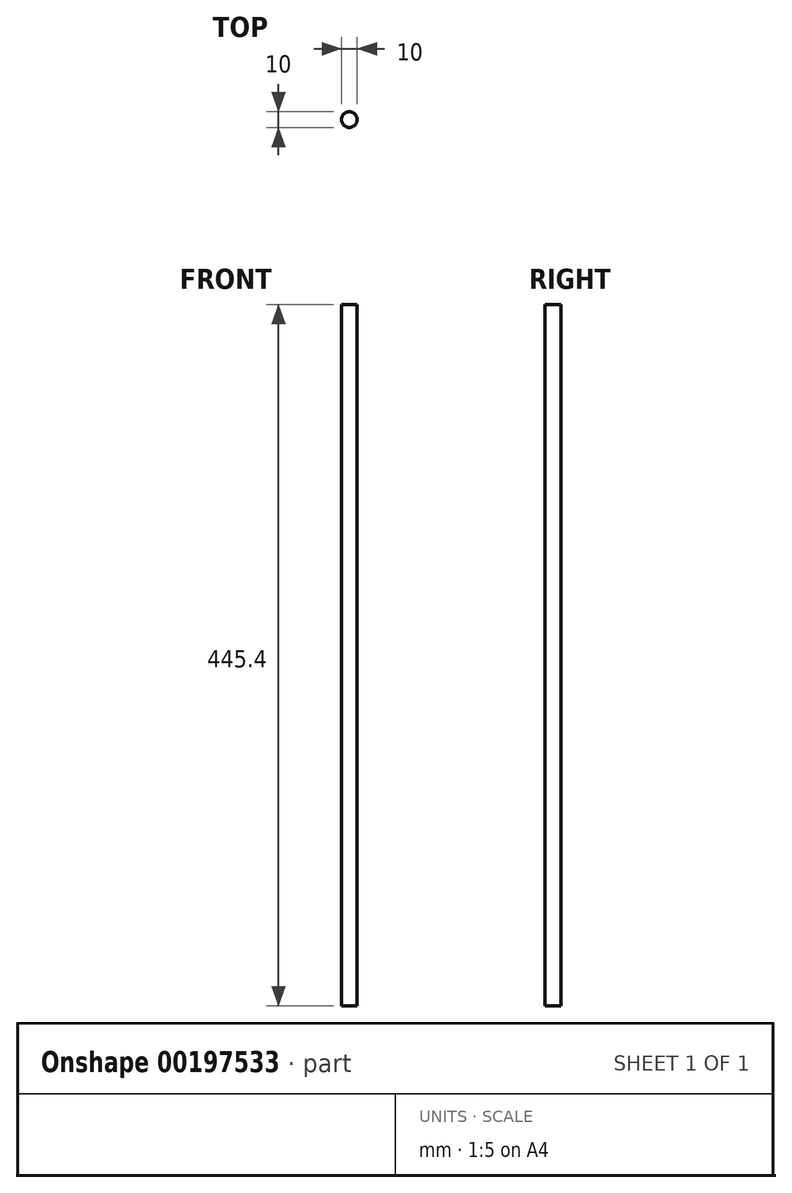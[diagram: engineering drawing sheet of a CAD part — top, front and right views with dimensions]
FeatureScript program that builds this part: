
annotation { "Feature Type Name" : "Feature", "Feature Type Description" : "" }
export const myFeature = defineFeature(function(context is Context, id is Id, definition is map)
    precondition{}
    {
        {
            var Q0;
            Q0=qCreatedBy(makeId("Top.planeOp"),FACE);
            var sketch = newSketch(context, id + "F0", { "sketchPlane" : qUnion([Q0])});
            skCircle(sketch, "E0", {"center": v(0, 0) * mm, "radius": 5 * mm});
            skSolve(sketch);
        }
        {
            var Q0;
            Q0=qSketchRegion(id+"F0",true);
            extrude(context, id + "F1", {"entities" : qUnion([Q0]), "depth" : 445.4 * mm});
        }
    });
